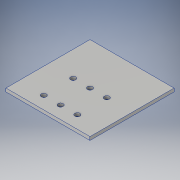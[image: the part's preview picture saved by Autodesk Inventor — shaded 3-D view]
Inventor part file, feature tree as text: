
AUTODESK INVENTOR PART (.ipt)
format: ipt  version: 2019 (Build 230136000, 136)  size: 122,368 bytes
history: native  units: mm
features: sketch x2, other x1, extrude x1, hole x1
ambient origin geometry x8: Origin, YZ Plane, XZ Plane, XY Plane, X Axis, Y Axis, Z Axis, Center Point
bodies: Body1 (feature_tree)
feature tree (5):
  other  "ソリッド1"
  extrude  "押し出し1"  Depth=50.0mm
  hole  "穴1"  [1 undecoded]
  sketch  "スケッチ1"
  sketch  "スケッチ2"
note: 1 required parameter value undecoded (feature->parameter linkage not recoverable at this tier; creation-order binding heuristic only, values carry confidence <= 0.55)
